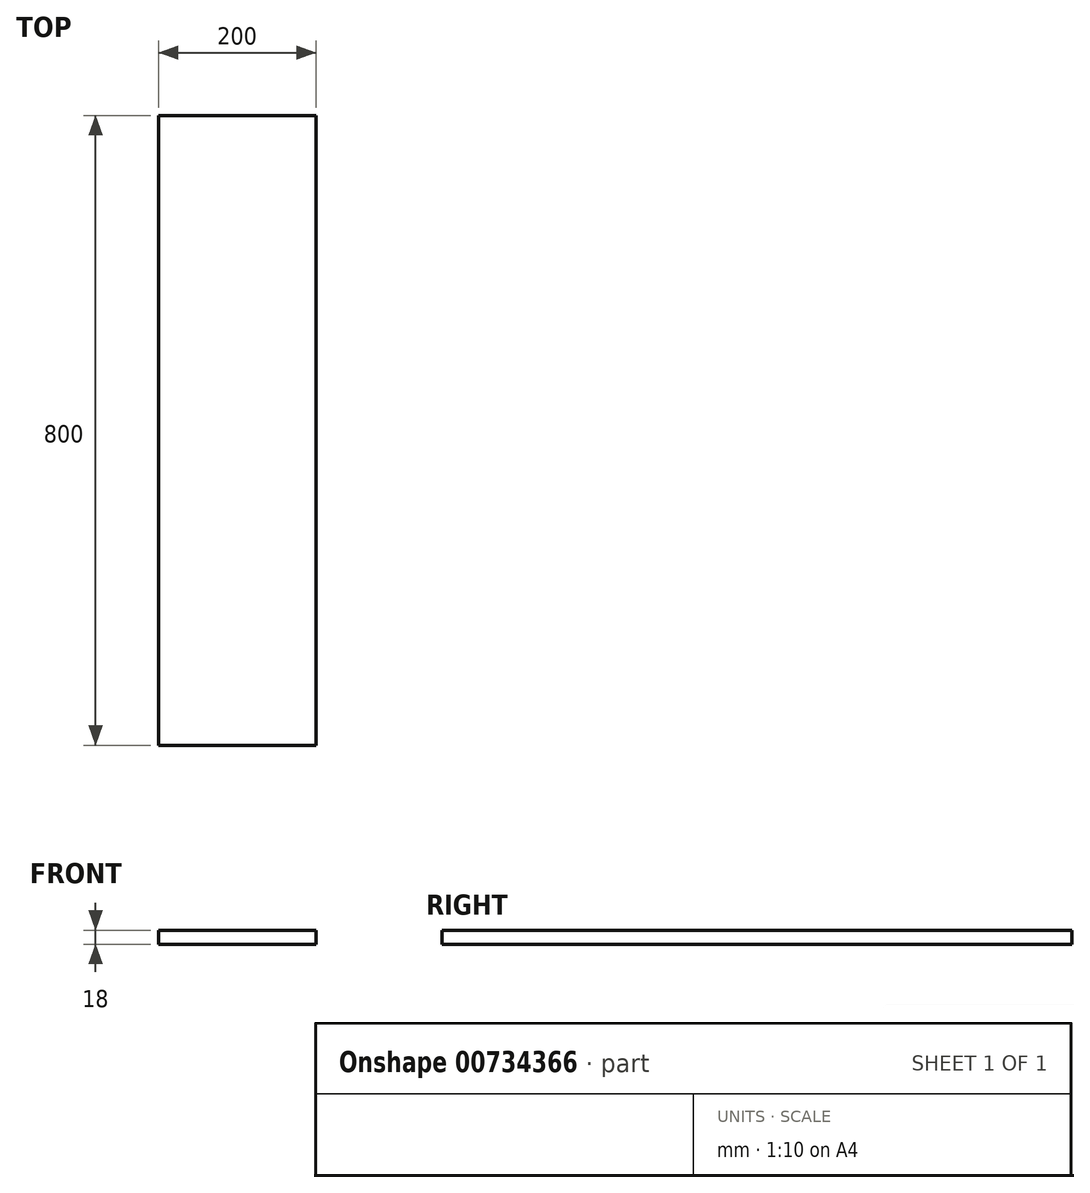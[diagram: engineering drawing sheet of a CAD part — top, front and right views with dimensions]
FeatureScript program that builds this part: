
annotation { "Feature Type Name" : "Feature", "Feature Type Description" : "" }
export const myFeature = defineFeature(function(context is Context, id is Id, definition is map)
    precondition{}
    {
        {
            var Q0;
            Q0=qCreatedBy(makeId("Top.planeOp"),FACE);
            var sketch = newSketch(context, id + "F0", { "sketchPlane" : qUnion([Q0])});
            skLineSegment(sketch, "E0.bottom", {"start": v(-100, -400) * mm, "end": v(100, -400) * mm});
            skLineSegment(sketch, "E0.top", {"start": v(-100, 400) * mm, "end": v(100, 400) * mm});
            skLineSegment(sketch, "E0.left", {"start": v(-100, -400) * mm, "end": v(-100, 400) * mm});
            skLineSegment(sketch, "E0.right", {"start": v(100, -400) * mm, "end": v(100, 400) * mm});
            skPoint(sketch, "E0.middle", {"position": v(0, 0) * mm});
            skSolve(sketch);
        }
        {
            var Q0;
            Q0 = qSketchRegion(id + "F0", true);
            extrude(context, id + "F1", {"entities" : qUnion([Q0]), "depth" : 18 * mm, "offsetDistance" : 25 * mm});
        }
    });
